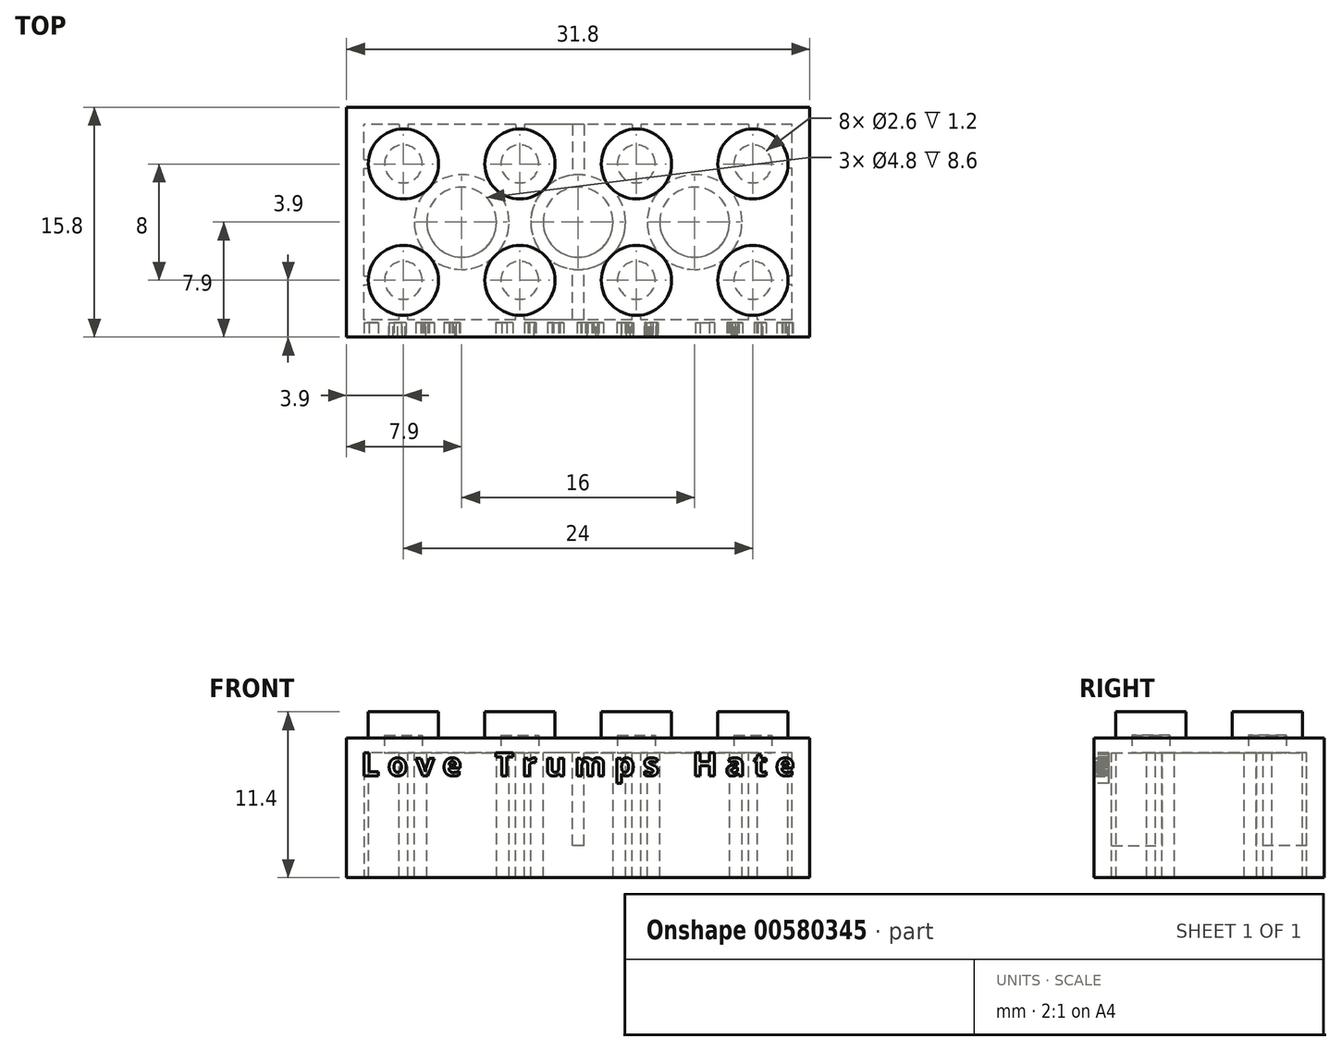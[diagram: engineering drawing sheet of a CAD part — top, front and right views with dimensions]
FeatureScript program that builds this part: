
annotation { "Feature Type Name" : "Feature", "Feature Type Description" : "" }
export const myFeature = defineFeature(function(context is Context, id is Id, definition is map)
    precondition{}
    {
        {
            var Q0;
            Q0=qCreatedBy(makeId("Top.planeOp"),FACE);
            var sketch = newSketch(context, id + "F0", { "sketchPlane" : qUnion([Q0])});
            skLineSegment(sketch, "E0.bottom", {"start": v(-15.9, -7.9) * mm, "end": v(15.9, -7.9) * mm});
            skLineSegment(sketch, "E0.top", {"start": v(-15.9, 7.9) * mm, "end": v(15.9, 7.9) * mm});
            skLineSegment(sketch, "E0.left", {"start": v(-15.9, -7.9) * mm, "end": v(-15.9, 7.9) * mm});
            skLineSegment(sketch, "E0.right", {"start": v(15.9, -7.9) * mm, "end": v(15.9, 7.9) * mm});
            skSolve(sketch);
        }
        {
            var Q0;
            Q0 = qSketchRegion(id + "F0", true);
            extrude(context, id + "F1", {"entities" : qUnion([Q0]), "endBound" : BoundingType.SYMMETRIC, "oppositeDirection" : true, "depth" : 9.6 * mm, "offsetDistance" : 25 * mm});
        }
        {
            var Q0;
            Q0=makeQuery(id+"F1.opExtrude","CAP_FACE",FACE,{"disambiguationData":[OSD([sQuery(id+"F0.wireOp",EDGE,"E0.bottom"),sQuery(id+"F0.wireOp",EDGE,"E0.top"),sQuery(id+"F0.wireOp",EDGE,"E0.left"),sQuery(id+"F0.wireOp",EDGE,"E0.right")])],"isStart":false});
            var sketch = newSketch(context, id + "F2", { "sketchPlane" : qUnion([Q0])});
            skLineSegment(sketch, "E1.bottom", {"start": v(14.7, 6.7) * mm, "end": v(-14.7, 6.7) * mm});
            skLineSegment(sketch, "E1.top", {"start": v(14.7, -6.7) * mm, "end": v(-14.7, -6.7) * mm});
            skLineSegment(sketch, "E1.left", {"start": v(14.7, 6.7) * mm, "end": v(14.7, -6.7) * mm});
            skLineSegment(sketch, "E1.right", {"start": v(-14.7, 6.7) * mm, "end": v(-14.7, -6.7) * mm});
            skPoint(sketch, "E1.middle", {"position": v(0, 0) * mm});
            skSolve(sketch);
        }
        {
            var Q0;
            Q0=makeQuery(id+"F2.imprint","IMPRINT",FACE,{"disambiguationData":[TD([[makeQuery(id+"F2.imprint","IMPRINT",EDGE,{"derivedFrom":sQuery(id+"F2.wireOp",EDGE,"E1.bottom")}),1.0]])]});
            extrude(context, id + "F3", {"entities" : qUnion([Q0]), "operationType" : NewBodyOperationType.REMOVE, "oppositeDirection" : true, "depth" : 8.6 * mm, "offsetDistance" : 25 * mm});
        }
        {
            var Q0;
            Q0=makeQuery(id+"F1.opExtrude","CAP_FACE",FACE,{"disambiguationData":[OSD([sQuery(id+"F0.wireOp",EDGE,"E0.bottom"),sQuery(id+"F0.wireOp",EDGE,"E0.top"),sQuery(id+"F0.wireOp",EDGE,"E0.left"),sQuery(id+"F0.wireOp",EDGE,"E0.right")])],"isStart":true});
            var sketch = newSketch(context, id + "F4", { "sketchPlane" : qUnion([Q0])});
            skCircle(sketch, "E2", {"center": v(-12, 4) * mm, "radius": 2.4 * mm});
            skCircle(sketch, "E3", {"center": v(-4, 4) * mm, "radius": 2.4 * mm});
            skCircle(sketch, "E4.MirrorC", {"center": v(-12, -4) * mm, "radius": 2.4 * mm});
            skCircle(sketch, "E5.MirrorC", {"center": v(-4, -4) * mm, "radius": 2.4 * mm});
            skCircle(sketch, "E6.MirrorC", {"center": v(4, -4) * mm, "radius": 2.4 * mm});
            skCircle(sketch, "E7.MirrorC", {"center": v(12, -4) * mm, "radius": 2.4 * mm});
            skCircle(sketch, "E8.MirrorC", {"center": v(4, 4) * mm, "radius": 2.4 * mm});
            skCircle(sketch, "E9.MirrorC", {"center": v(12, 4) * mm, "radius": 2.4 * mm});
            skSolve(sketch);
        }
        {
            var Q0;
            Q0 = qSketchRegion(id + "F4", true);
            extrude(context, id + "F5", {"entities" : qUnion([Q0]), "operationType" : NewBodyOperationType.ADD, "depth" : 1.8 * mm, "offsetDistance" : 25 * mm});
        }
        {
            var Q0;
            Q0=makeQuery(id+"F3.boolean.opBoolean","COPY",FACE,{"derivedFrom":makeQuery(id+"F3.opExtrude","CAP_FACE",FACE,{"disambiguationData":[OSD([sQuery(id+"F2.wireOp",EDGE,"E1.bottom"),sQuery(id+"F2.wireOp",EDGE,"E1.top"),sQuery(id+"F2.wireOp",EDGE,"E1.left"),sQuery(id+"F2.wireOp",EDGE,"E1.right")])],"isStart":false})});
            var sketch = newSketch(context, id + "F6", { "sketchPlane" : qUnion([Q0])});
            skCircle(sketch, "E10", {"center": v(-12, 4) * mm, "radius": 1.3 * mm});
            skCircle(sketch, "E11", {"center": v(-4, 4) * mm, "radius": 1.3 * mm});
            skCircle(sketch, "E12.MirrorC", {"center": v(-4, -4) * mm, "radius": 1.3 * mm});
            skCircle(sketch, "E13.MirrorC", {"center": v(-12, -4) * mm, "radius": 1.3 * mm});
            skCircle(sketch, "E14.MirrorC", {"center": v(4, -4) * mm, "radius": 1.3 * mm});
            skCircle(sketch, "E15.MirrorC", {"center": v(12, -4) * mm, "radius": 1.3 * mm});
            skCircle(sketch, "E16.MirrorC", {"center": v(4, 4) * mm, "radius": 1.3 * mm});
            skCircle(sketch, "E17.MirrorC", {"center": v(12, 4) * mm, "radius": 1.3 * mm});
            skSolve(sketch);
        }
        {
            var Q0;
            Q0 = qSketchRegion(id + "F6", true);
            extrude(context, id + "F7", {"entities" : qUnion([Q0]), "operationType" : NewBodyOperationType.REMOVE, "oppositeDirection" : true, "depth" : 1.2 * mm, "offsetDistance" : 25 * mm});
        }
        {
            var Q0;
            Q0=makeQuery(id+"F3.boolean.opBoolean","COPY",FACE,{"derivedFrom":makeQuery(id+"F3.opExtrude","CAP_FACE",FACE,{"disambiguationData":[OSD([sQuery(id+"F2.wireOp",EDGE,"E1.bottom"),sQuery(id+"F2.wireOp",EDGE,"E1.top"),sQuery(id+"F2.wireOp",EDGE,"E1.left"),sQuery(id+"F2.wireOp",EDGE,"E1.right")])],"isStart":false})});
            var sketch = newSketch(context, id + "F8", { "sketchPlane" : qUnion([Q0])});
            skPoint(sketch, "E18", {"position": v(-12, 4) * mm});
            skPoint(sketch, "E19", {"position": v(-4, 4) * mm});
            skPoint(sketch, "E20", {"position": v(4, 4) * mm});
            skPoint(sketch, "E21", {"position": v(12, 4) * mm});
            skPoint(sketch, "E22", {"position": v(12, -4) * mm});
            skPoint(sketch, "E23", {"position": v(4, -4) * mm});
            skPoint(sketch, "E24", {"position": v(-4, -4) * mm});
            skPoint(sketch, "E25", {"position": v(-12, -4) * mm});
            skLineSegment(sketch, "E26", {"start": v(-12, 4) * mm, "end": v(-4, -4) * mm, "construction": true});
            skLineSegment(sketch, "E27", {"start": v(-4, 4) * mm, "end": v(-12, -4) * mm, "construction": true});
            skLineSegment(sketch, "E28", {"start": v(4, 4) * mm, "end": v(12, -4) * mm, "construction": true});
            skLineSegment(sketch, "E29", {"start": v(12, 4) * mm, "end": v(4, -4) * mm, "construction": true});
            skLineSegment(sketch, "E30", {"start": v(-4, 4) * mm, "end": v(4, -4) * mm, "construction": true});
            skLineSegment(sketch, "E31", {"start": v(4, 4) * mm, "end": v(-4, -4) * mm, "construction": true});
            skLineSegment(sketch, "E32", {"start": v(-12, -4) * mm, "end": v(-4, 4) * mm, "construction": true});
            skCircle(sketch, "E33", {"center": v(-8, 0) * mm, "radius": 3.25 * mm});
            skCircle(sketch, "E34", {"center": v(0, 0) * mm, "radius": 3.25 * mm});
            skCircle(sketch, "E35", {"center": v(8, 0) * mm, "radius": 3.25 * mm});
            skCircle(sketch, "E36", {"center": v(-8, 0) * mm, "radius": 2.4 * mm});
            skCircle(sketch, "E37", {"center": v(0, 0) * mm, "radius": 2.4 * mm});
            skCircle(sketch, "E38", {"center": v(8, 0) * mm, "radius": 2.4 * mm});
            skSolve(sketch);
        }
        {
            var Q0;
            Q0=makeQuery(id+"F8.imprint","IMPRINT",FACE,{"disambiguationData":[TD([[makeQuery(id+"F8.imprint","IMPRINT",EDGE,{"derivedFrom":sQuery(id+"F8.wireOp",EDGE,"E33")}),1.0]])]});
            var Q1;
            Q1=makeQuery(id+"F8.imprint","IMPRINT",FACE,{"disambiguationData":[TD([[makeQuery(id+"F8.imprint","IMPRINT",EDGE,{"derivedFrom":sQuery(id+"F8.wireOp",EDGE,"E34")}),1.0]])]});
            var Q2;
            Q2=makeQuery(id+"F8.imprint","IMPRINT",FACE,{"disambiguationData":[TD([[makeQuery(id+"F8.imprint","IMPRINT",EDGE,{"derivedFrom":sQuery(id+"F8.wireOp",EDGE,"E35")}),1.0]])]});
            var Q3;
            Q3=makeQuery(id+"F1.opExtrude","CAP_FACE",FACE,{"disambiguationData":[OSD([sQuery(id+"F0.wireOp",EDGE,"E0.bottom"),sQuery(id+"F0.wireOp",EDGE,"E0.top"),sQuery(id+"F0.wireOp",EDGE,"E0.left"),sQuery(id+"F0.wireOp",EDGE,"E0.right")])],"isStart":false});
            extrude(context, id + "F9", {"entities" : qUnion([Q0, Q1, Q2]), "operationType" : NewBodyOperationType.ADD, "endBound" : BoundingType.UP_TO_SURFACE, "depth" : 25 * mm, "endBoundEntityFace" : qUnion([Q3]), "offsetDistance" : 25 * mm});
        }
        {
            var Q0;
            {var subQ0=sQuery(id+"F2.wireOp",EDGE,"E1.left");var subQ1=sQuery(id+"F2.wireOp",EDGE,"E1.bottom");var subQ2=sQuery(id+"F2.wireOp",EDGE,"E1.top");var subQ3=sQuery(id+"F2.wireOp",EDGE,"E1.right");Q0=makeQuery(id+"F9.boolean.opBoolean","SPLIT",FACE,{"disambiguationData":[TD([makeQuery(id+"F3.boolean.opBoolean","COPY",FACE,{"derivedFrom":makeQuery(id+"F3.opExtrude","SWEPT_FACE",FACE,{"disambiguationData":[OSD([subQ1])]})})])],"derivedFrom":makeQuery(id+"F3.boolean.opBoolean","COPY",FACE,{"derivedFrom":makeQuery(id+"F3.opExtrude","CAP_FACE",FACE,{"disambiguationData":[OSD([subQ1,subQ2,subQ0,subQ3])],"isStart":false})})});}
            var sketch = newSketch(context, id + "F10", { "sketchPlane" : qUnion([Q0])});
            skPoint(sketch, "E39", {"position": v(-12, 4) * mm});
            skLineSegment(sketch, "E40", {"start": v(-12, 4) * mm, "end": v(-15.6, 4) * mm, "construction": true});
            skLineSegment(sketch, "E41.bottom", {"start": v(-14.7, 3.7) * mm, "end": v(-14.4, 3.7) * mm});
            skLineSegment(sketch, "E41.top", {"start": v(-14.7, 4.3) * mm, "end": v(-14.4, 4.3) * mm});
            skLineSegment(sketch, "E41.left", {"start": v(-14.7, 3.7) * mm, "end": v(-14.7, 4.3) * mm});
            skLineSegment(sketch, "E41.right", {"start": v(-14.4, 3.7) * mm, "end": v(-14.4, 4.3) * mm});
            skLineSegment(sketch, "E42.top", {"start": v(-14.4, 4.2) * mm, "end": v(-14.4, 4.2) * mm});
            skLineSegment(sketch, "E42.left", {"start": v(-14.4, 4.26) * mm, "end": v(-14.4, 4.2) * mm});
            skLineSegment(sketch, "E42.right", {"start": v(-14.4, 4.26) * mm, "end": v(-14.4, 4.2) * mm});
            skLineSegment(sketch, "E43.MirrorCS", {"start": v(-14.4, -3.7) * mm, "end": v(-14.4, -4.3) * mm});
            skLineSegment(sketch, "E44.MirrorCS", {"start": v(-14.7, -4.3) * mm, "end": v(-14.4, -4.3) * mm});
            skLineSegment(sketch, "E45.MirrorCS", {"start": v(-14.7, -3.7) * mm, "end": v(-14.7, -4.3) * mm});
            skLineSegment(sketch, "E46.MirrorCS", {"start": v(-14.7, -3.7) * mm, "end": v(-14.4, -3.7) * mm});
            skLineSegment(sketch, "E47.MirrorCS", {"start": v(14.7, -3.7) * mm, "end": v(14.4, -3.7) * mm});
            skLineSegment(sketch, "E48.MirrorCS", {"start": v(14.7, -3.7) * mm, "end": v(14.7, -4.3) * mm});
            skLineSegment(sketch, "E49.MirrorCS", {"start": v(14.4, -3.7) * mm, "end": v(14.4, -4.3) * mm});
            skLineSegment(sketch, "E50.MirrorCS", {"start": v(14.7, -4.3) * mm, "end": v(14.4, -4.3) * mm});
            skLineSegment(sketch, "E51.MirrorCS", {"start": v(14.7, 3.7) * mm, "end": v(14.7, 4.3) * mm});
            skLineSegment(sketch, "E52.MirrorCS", {"start": v(14.4, 3.7) * mm, "end": v(14.4, 4.3) * mm});
            skLineSegment(sketch, "E53.MirrorCS", {"start": v(14.7, 3.7) * mm, "end": v(14.4, 3.7) * mm});
            skLineSegment(sketch, "E54.MirrorCS", {"start": v(14.7, 4.3) * mm, "end": v(14.4, 4.3) * mm});
            skPoint(sketch, "E55.MirrorP", {"position": v(12, 4) * mm});
            skLineSegment(sketch, "E56", {"start": v(-12, 4) * mm, "end": v(-12, 8.85) * mm, "construction": true});
            skSolve(sketch);
        }
        {
            var Q0;
            Q0 = qSketchRegion(id + "F10", true);
            var Q1;
            Q1=makeQuery(id+"F1.opExtrude","CAP_FACE",FACE,{"disambiguationData":[OSD([sQuery(id+"F0.wireOp",EDGE,"E0.bottom"),sQuery(id+"F0.wireOp",EDGE,"E0.top"),sQuery(id+"F0.wireOp",EDGE,"E0.left"),sQuery(id+"F0.wireOp",EDGE,"E0.right")])],"isStart":false});
            extrude(context, id + "F11", {"entities" : qUnion([Q0]), "operationType" : NewBodyOperationType.ADD, "endBound" : BoundingType.UP_TO_SURFACE, "depth" : 25 * mm, "endBoundEntityFace" : qUnion([Q1]), "offsetDistance" : 25 * mm});
        }
        {
            var Q0;
            {var subQ0=sQuery(id+"F2.wireOp",EDGE,"E1.left");var subQ1=sQuery(id+"F2.wireOp",EDGE,"E1.bottom");var subQ2=sQuery(id+"F2.wireOp",EDGE,"E1.top");var subQ3=sQuery(id+"F2.wireOp",EDGE,"E1.right");Q0=makeQuery(id+"F9.boolean.opBoolean","SPLIT",FACE,{"disambiguationData":[TD([makeQuery(id+"F3.boolean.opBoolean","COPY",FACE,{"derivedFrom":makeQuery(id+"F3.opExtrude","SWEPT_FACE",FACE,{"disambiguationData":[OSD([subQ1])]})})])],"derivedFrom":makeQuery(id+"F3.boolean.opBoolean","COPY",FACE,{"derivedFrom":makeQuery(id+"F3.opExtrude","CAP_FACE",FACE,{"disambiguationData":[OSD([subQ1,subQ2,subQ0,subQ3])],"isStart":false})})});}
            var sketch = newSketch(context, id + "F12", { "sketchPlane" : qUnion([Q0])});
            skPoint(sketch, "E57", {"position": v(-12, 4) * mm});
            skLineSegment(sketch, "E58", {"start": v(-12, 4) * mm, "end": v(-12, 7.3) * mm, "construction": true});
            skLineSegment(sketch, "E59.bottom", {"start": v(-12.3, 6.7) * mm, "end": v(-11.7, 6.7) * mm});
            skLineSegment(sketch, "E59.top", {"start": v(-12.3, 6.4) * mm, "end": v(-11.7, 6.4) * mm});
            skLineSegment(sketch, "E59.left", {"start": v(-12.3, 6.7) * mm, "end": v(-12.3, 6.4) * mm});
            skLineSegment(sketch, "E59.right", {"start": v(-11.7, 6.7) * mm, "end": v(-11.7, 6.4) * mm});
            skPoint(sketch, "E60", {"position": v(-8, 0) * mm});
            skLineSegment(sketch, "E61", {"start": v(-8, 0) * mm, "end": v(-8, 14.45) * mm, "construction": true});
            skLineSegment(sketch, "E62.MirrorCS", {"start": v(-3.7, 6.4) * mm, "end": v(-4.3, 6.4) * mm});
            skLineSegment(sketch, "E63.MirrorCS", {"start": v(-3.7, 6.7) * mm, "end": v(-3.7, 6.4) * mm});
            skLineSegment(sketch, "E64.MirrorCS", {"start": v(-3.7, 6.7) * mm, "end": v(-4.3, 6.7) * mm});
            skLineSegment(sketch, "E65.MirrorCS", {"start": v(-4.3, 6.7) * mm, "end": v(-4.3, 6.4) * mm});
            skLineSegment(sketch, "E66.MirrorCS", {"start": v(3.7, 6.7) * mm, "end": v(3.7, 6.4) * mm});
            skLineSegment(sketch, "E67.MirrorCS", {"start": v(3.7, 6.7) * mm, "end": v(4.3, 6.7) * mm});
            skLineSegment(sketch, "E68.MirrorCS", {"start": v(4.3, 6.7) * mm, "end": v(4.3, 6.4) * mm});
            skLineSegment(sketch, "E69.MirrorCS", {"start": v(3.7, 6.4) * mm, "end": v(4.3, 6.4) * mm});
            skLineSegment(sketch, "E70.MirrorCS", {"start": v(12.3, 6.7) * mm, "end": v(11.7, 6.7) * mm});
            skLineSegment(sketch, "E71.MirrorCS", {"start": v(11.7, 6.7) * mm, "end": v(11.7, 6.4) * mm});
            skLineSegment(sketch, "E72.MirrorCS", {"start": v(12.3, 6.4) * mm, "end": v(11.7, 6.4) * mm});
            skLineSegment(sketch, "E73.MirrorCS", {"start": v(12.3, 6.7) * mm, "end": v(12.3, 6.4) * mm});
            skLineSegment(sketch, "E74.MirrorCS", {"start": v(-4.3, -6.7) * mm, "end": v(-4.3, -6.4) * mm});
            skLineSegment(sketch, "E75.MirrorCS", {"start": v(-3.7, -6.7) * mm, "end": v(-4.3, -6.7) * mm});
            skLineSegment(sketch, "E76.MirrorCS", {"start": v(-3.7, -6.7) * mm, "end": v(-3.7, -6.4) * mm});
            skLineSegment(sketch, "E77.MirrorCS", {"start": v(-3.7, -6.4) * mm, "end": v(-4.3, -6.4) * mm});
            skLineSegment(sketch, "E78.MirrorCS", {"start": v(-11.7, -6.7) * mm, "end": v(-11.7, -6.4) * mm});
            skLineSegment(sketch, "E79.MirrorCS", {"start": v(-12.3, -6.7) * mm, "end": v(-11.7, -6.7) * mm});
            skLineSegment(sketch, "E80.MirrorCS", {"start": v(-12.3, -6.7) * mm, "end": v(-12.3, -6.4) * mm});
            skLineSegment(sketch, "E81.MirrorCS", {"start": v(-12.3, -6.4) * mm, "end": v(-11.7, -6.4) * mm});
            skLineSegment(sketch, "E82.MirrorCS", {"start": v(3.7, -6.7) * mm, "end": v(4.3, -6.7) * mm});
            skLineSegment(sketch, "E83.MirrorCS", {"start": v(3.7, -6.4) * mm, "end": v(4.3, -6.4) * mm});
            skLineSegment(sketch, "E84.MirrorCS", {"start": v(3.7, -6.7) * mm, "end": v(3.7, -6.4) * mm});
            skLineSegment(sketch, "E85.MirrorCS", {"start": v(4.3, -6.7) * mm, "end": v(4.3, -6.4) * mm});
            skLineSegment(sketch, "E86.MirrorCS", {"start": v(12.3, -6.4) * mm, "end": v(11.7, -6.4) * mm});
            skLineSegment(sketch, "E87.MirrorCS", {"start": v(12.3, -6.7) * mm, "end": v(11.7, -6.7) * mm});
            skLineSegment(sketch, "E88.MirrorCS", {"start": v(11.7, -6.7) * mm, "end": v(11.7, -6.4) * mm});
            skLineSegment(sketch, "E89.MirrorCS", {"start": v(12.3, -6.7) * mm, "end": v(12.3, -6.4) * mm});
            skSolve(sketch);
        }
        {
            var Q0;
            Q0 = qSketchRegion(id + "F12", true);
            var Q1;
            {var subQ0=sQuery(id+"F0.wireOp",EDGE,"E0.right");var subQ1=sQuery(id+"F0.wireOp",EDGE,"E0.left");var subQ2=sQuery(id+"F0.wireOp",EDGE,"E0.top");var subQ3=sQuery(id+"F0.wireOp",EDGE,"E0.bottom");Q1=makeQuery(id+"F11.boolean.opBoolean","MERGE",FACE,{"derivedFrom":[makeQuery(id+"F1.opExtrude","CAP_FACE",FACE,{"disambiguationData":[OSD([subQ3,subQ2,subQ1,subQ0])],"isStart":false}),makeQuery(id+"F11.opExtrude","CAP_FACE",FACE,{"disambiguationData":[OSD([subQ3,subQ2,subQ1,subQ0]),OD(0.0)],"isStart":false}),makeQuery(id+"F11.opExtrude","CAP_FACE",FACE,{"disambiguationData":[OSD([subQ3,subQ2,subQ1,subQ0]),OD(1.0)],"isStart":false}),makeQuery(id+"F11.opExtrude","CAP_FACE",FACE,{"disambiguationData":[OSD([subQ3,subQ2,subQ1,subQ0]),OD(2.0)],"isStart":false}),makeQuery(id+"F11.opExtrude","CAP_FACE",FACE,{"disambiguationData":[OSD([subQ3,subQ2,subQ1,subQ0]),OD(3.0)],"isStart":false})]});}
            extrude(context, id + "F13", {"entities" : qUnion([Q0]), "operationType" : NewBodyOperationType.ADD, "endBound" : BoundingType.UP_TO_SURFACE, "depth" : 25 * mm, "endBoundEntityFace" : qUnion([Q1]), "offsetDistance" : 25 * mm});
        }
        {
            var Q0;
            {var subQ0=sQuery(id+"F2.wireOp",EDGE,"E1.left");var subQ1=sQuery(id+"F2.wireOp",EDGE,"E1.bottom");var subQ2=sQuery(id+"F2.wireOp",EDGE,"E1.top");var subQ3=sQuery(id+"F2.wireOp",EDGE,"E1.right");Q0=makeQuery(id+"F9.boolean.opBoolean","SPLIT",FACE,{"disambiguationData":[TD([makeQuery(id+"F3.boolean.opBoolean","COPY",FACE,{"derivedFrom":makeQuery(id+"F3.opExtrude","SWEPT_FACE",FACE,{"disambiguationData":[OSD([subQ1])]})})])],"derivedFrom":makeQuery(id+"F3.boolean.opBoolean","COPY",FACE,{"derivedFrom":makeQuery(id+"F3.opExtrude","CAP_FACE",FACE,{"disambiguationData":[OSD([subQ1,subQ2,subQ0,subQ3])],"isStart":false})})});}
            var sketch = newSketch(context, id + "F14", { "sketchPlane" : qUnion([Q0])});
            skLineSegment(sketch, "E90.bottom", {"start": v(-0.4, 6.7) * mm, "end": v(0.4, 6.7) * mm});
            skLineSegment(sketch, "E90.top", {"start": v(-0.4, 3.23) * mm, "end": v(0.4, 3.23) * mm});
            skLineSegment(sketch, "E90.left", {"start": v(-0.4, 6.7) * mm, "end": v(-0.4, 3.23) * mm});
            skLineSegment(sketch, "E90.right", {"start": v(0.4, 6.7) * mm, "end": v(0.4, 3.23) * mm});
            skLineSegment(sketch, "E91.MirrorCS", {"start": v(0.4, -6.7) * mm, "end": v(0.4, -3.23) * mm});
            skLineSegment(sketch, "E92.MirrorCS", {"start": v(-0.4, -6.7) * mm, "end": v(0.4, -6.7) * mm});
            skLineSegment(sketch, "E93.MirrorCS", {"start": v(-0.4, -6.7) * mm, "end": v(-0.4, -3.23) * mm});
            skLineSegment(sketch, "E94.MirrorCS", {"start": v(-0.4, -3.23) * mm, "end": v(0.4, -3.23) * mm});
            skSolve(sketch);
        }
        {
            var Q0;
            Q0 = qSketchRegion(id + "F14", true);
            extrude(context, id + "F15", {"entities" : qUnion([Q0]), "operationType" : NewBodyOperationType.ADD, "depth" : 6.4 * mm, "offsetDistance" : 25 * mm});
        }
        {
            var Q0;
            Q0=makeQuery(id+"F1.opExtrude","SWEPT_FACE",FACE,{"disambiguationData":[OSD([sQuery(id+"F0.wireOp",EDGE,"E0.bottom")])]});
            var sketch = newSketch(context, id + "F16", { "sketchPlane" : qUnion([Q0])});
            skText(sketch, "E95", { "text": "L o v e    T r u m p s    H a t e\n", "fontName": "OpenSans-Bold.ttf"});
            const initialGuessF16  = {"E95": [-0.0149, 0.00221, 1, 0, 0.00159]};
            skSetInitialGuess(sketch, initialGuessF16);
            skSolve(sketch);
        }
        {
            var Q0;
            Q0 = qSketchRegion(id + "F16", true);
            extrude(context, id + "F17", {"entities" : qUnion([Q0]), "operationType" : NewBodyOperationType.REMOVE, "oppositeDirection" : true, "depth" : 1 * mm, "offsetDistance" : 25 * mm});
        }
    });
